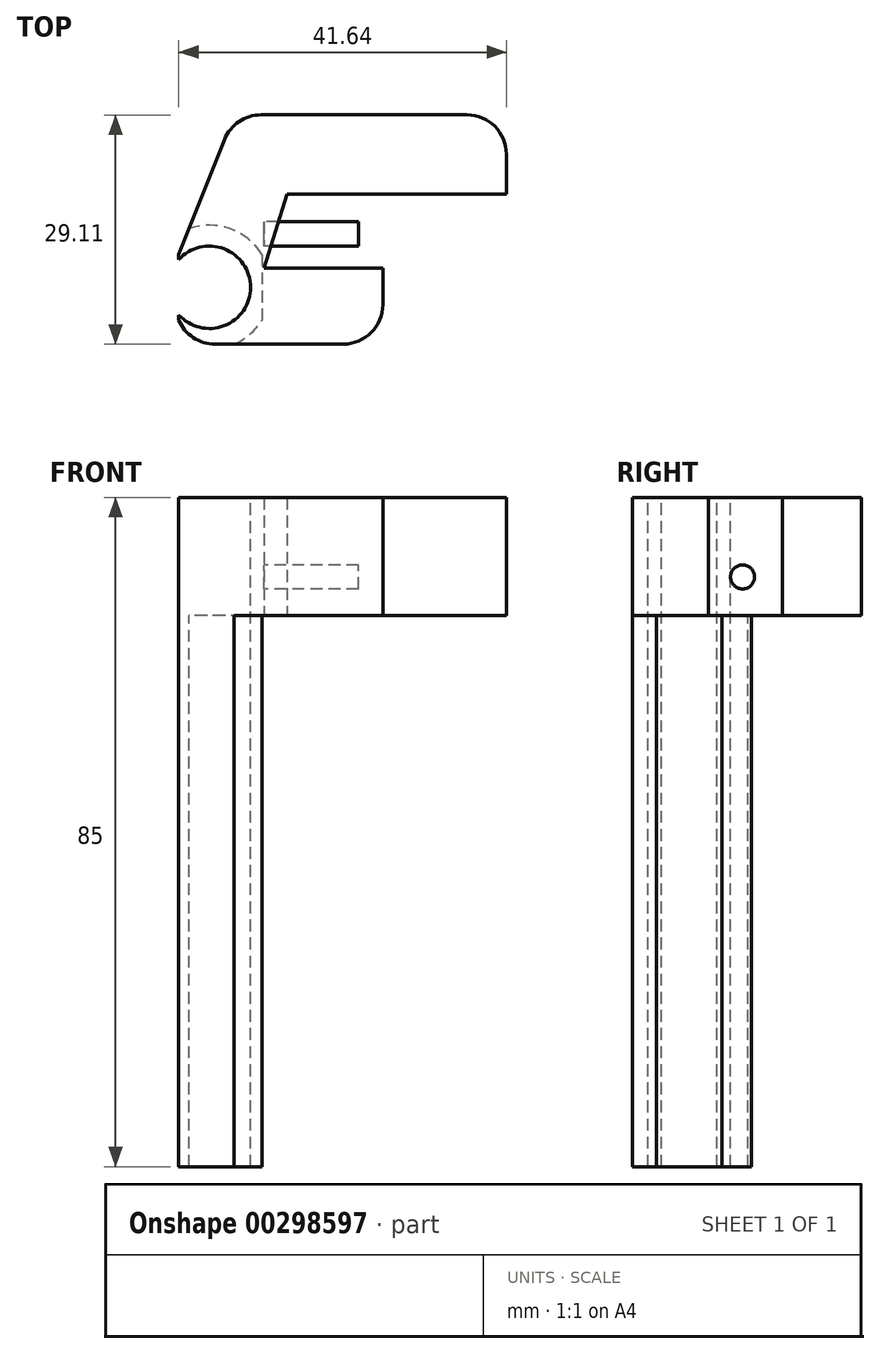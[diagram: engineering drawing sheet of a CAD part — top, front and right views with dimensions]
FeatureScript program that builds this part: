
annotation { "Feature Type Name" : "Feature", "Feature Type Description" : "" }
export const myFeature = defineFeature(function(context is Context, id is Id, definition is map)
    precondition{}
    {
        {
            var Q0;
            Q0=qCreatedBy(makeId("Top.planeOp"),FACE);
            var sketch = newSketch(context, id + "F0", { "sketchPlane" : qUnion([Q0])});
            skLineSegment(sketch, "E0", {"start": v(0, 0) * mm, "end": v(10.08, 0) * mm});
            skLineSegment(sketch, "E1", {"start": v(15.08, 5) * mm, "end": v(15.08, 9.63) * mm});
            skLineSegment(sketch, "E2", {"start": v(15.08, 9.63) * mm, "end": v(0, 9.63) * mm});
            skLineSegment(sketch, "E3", {"start": v(0, 9.63) * mm, "end": v(2.93, 19.06) * mm});
            skLineSegment(sketch, "E4", {"start": v(2.93, 19.06) * mm, "end": v(30.79, 19.06) * mm});
            skLineSegment(sketch, "E5", {"start": v(30.79, 19.06) * mm, "end": v(30.79, 24.11) * mm});
            skLineSegment(sketch, "E6", {"start": v(25.79, 29.11) * mm, "end": v(-0.37, 29.11) * mm});
            skLineSegment(sketch, "E7", {"start": v(-5.01, 25.97) * mm, "end": v(-10.85, 11.39) * mm});
            skLineSegment(sketch, "E8", {"start": v(-6.23, 0) * mm, "end": v(0, 0) * mm});
            skPoint(sketch, "E9.visualSharp", {"position": v(-3.76, 29.11) * mm});
            skArc(sketch, "E9.filletArc", {"start": v(-0.37, 29.11) * mm, "mid": v(-3.17, 28.25) * mm, "end": v(-5.01, 25.97) * mm});
            skPoint(sketch, "E10.visualSharp", {"position": v(30.79, 29.11) * mm});
            skArc(sketch, "E10.filletArc", {"start": v(30.79, 24.11) * mm, "mid": v(29.32, 27.65) * mm, "end": v(25.79, 29.11) * mm});
            skPoint(sketch, "E11.visualSharp", {"position": v(15.08, 0) * mm});
            skArc(sketch, "E11.filletArc", {"start": v(10.08, 0) * mm, "mid": v(13.62, 1.46) * mm, "end": v(15.08, 5) * mm});
            skPoint(sketch, "E12.visualSharp", {"position": v(4.77, 0) * mm});
            skArc(sketch, "E12.filletArc", {"start": v(-10.84, 3.05) * mm, "mid": v(-9, 0.83) * mm, "end": v(-6.23, 0) * mm});
            skCircle(sketch, "E13", {"center": v(-6.95, 7.22) * mm, "radius": 5.23 * mm});
            skArc(sketch, "E14", {"start": v(-0.27, 11.39) * mm, "mid": v(-14.83, 7.2) * mm, "end": v(-0.26, 3.05) * mm});
            skLineSegment(sketch, "E15.bottom", {"start": v(-18.29, 9.54) * mm, "end": v(-7.98, 9.54) * mm});
            skLineSegment(sketch, "E15.top", {"start": v(-18.29, 5) * mm, "end": v(-7.98, 5) * mm});
            skLineSegment(sketch, "E15.left", {"start": v(-18.29, 9.54) * mm, "end": v(-18.29, 5) * mm});
            skLineSegment(sketch, "E15.right", {"start": v(-7.98, 9.54) * mm, "end": v(-7.98, 5) * mm});
            skLineSegment(sketch, "E16", {"start": v(-0.27, 11.39) * mm, "end": v(-0.26, 3.05) * mm});
            skLineSegment(sketch, "E17", {"start": v(-10.85, 11.39) * mm, "end": v(-10.84, 3.05) * mm});
            skSolve(sketch);
        }
        {
            var Q0;
            Q0=makeQuery(id+"F0.imprint","IMPRINT",FACE,{"disambiguationData":[TD([[makeQuery(id+"F0.imprint","IMPRINT",EDGE,{"derivedFrom":sQuery(id+"F0.wireOp",EDGE,"E0")}),1.0]])]});
            extrude(context, id + "F1", {"entities" : qUnion([Q0]), "depth" : 15 * mm});
        }
        {
            var Q0;
            Q0=qCreatedBy(makeId("Right.planeOp"),FACE);
            var sketch = newSketch(context, id + "F2", { "sketchPlane" : qUnion([Q0])});
            skCircle(sketch, "E18", {"center": v(14, 4.92) * mm, "radius": 1.53 * mm});
            skSolve(sketch);
        }
        {
            var Q0;
            Q0 = qSketchRegion(id + "F2", true);
            extrude(context, id + "F3", {"entities" : qUnion([Q0]), "depth" : 12 * mm});
        }
        {
            var Q0;
            {var subQ0=sQuery(id+"F0.wireOp",EDGE,"E16");Q0=makeQuery(id+"F0.imprint","IMPRINT",FACE,{"disambiguationData":[TD([[makeQuery(id+"F0.imprint","IMPRINT",EDGE,{"derivedFrom":subQ0}),-1.0]])]});}
            extrude(context, id + "F4", {"entities" : qUnion([Q0]), "operationType" : NewBodyOperationType.ADD, "oppositeDirection" : true, "depth" : 70 * mm, "hasSecondDirection" : true, "secondDirectionOppositeDirection" : false, "secondDirectionDepth" : 15 * mm});
        }
        {
            var Q0;
            {var subQ0=sQuery(id+"F0.wireOp",EDGE,"E15.right");Q0=makeQuery(id+"F0.imprint","IMPRINT",FACE,{"disambiguationData":[TD([[makeQuery(id+"F0.imprint","IMPRINT",EDGE,{"derivedFrom":subQ0}),1.0]])]});}
            var Q1;
            {var subQ0=sQuery(id+"F0.wireOp",EDGE,"E15.right");Q1=makeQuery(id+"F0.imprint","IMPRINT",FACE,{"disambiguationData":[TD([[makeQuery(id+"F0.imprint","IMPRINT",EDGE,{"derivedFrom":subQ0}),-1.0]])]});}
            extrude(context, id + "F5", {"entities" : qUnion([Q0, Q1]), "operationType" : NewBodyOperationType.REMOVE, "depth" : 25 * mm, "hasSecondDirection" : true, "secondDirectionOppositeDirection" : false, "secondDirectionDepth" : 15 * mm});
        }
    });
